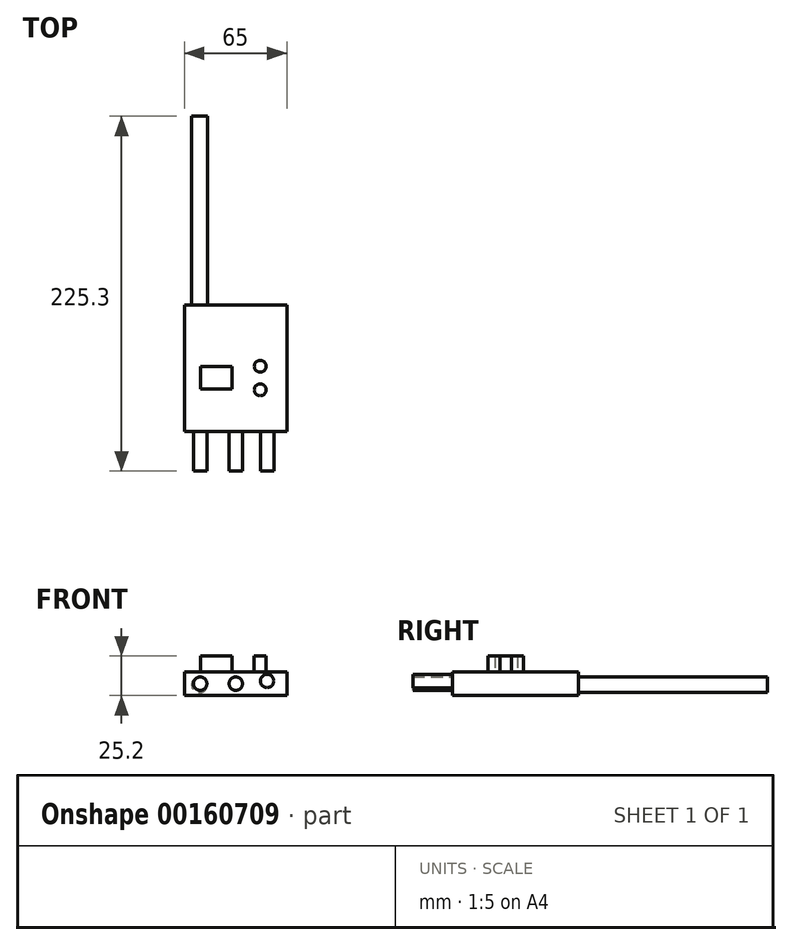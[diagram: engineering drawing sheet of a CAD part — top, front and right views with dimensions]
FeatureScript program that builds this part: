
annotation { "Feature Type Name" : "Feature", "Feature Type Description" : "" }
export const myFeature = defineFeature(function(context is Context, id is Id, definition is map)
    precondition{}
    {
        {
            var Q0;
            Q0=qCreatedBy(makeId("Top.planeOp"),FACE);
            var sketch = newSketch(context, id + "F0", { "sketchPlane" : qUnion([Q0])});
            skLineSegment(sketch, "E0.bottom", {"start": v(32.5, -40.15) * mm, "end": v(-32.5, -40.15) * mm});
            skLineSegment(sketch, "E0.top", {"start": v(32.5, 40.15) * mm, "end": v(-32.5, 40.15) * mm});
            skLineSegment(sketch, "E0.left", {"start": v(32.5, -40.15) * mm, "end": v(32.5, 40.15) * mm});
            skLineSegment(sketch, "E0.right", {"start": v(-32.5, -40.15) * mm, "end": v(-32.5, 40.15) * mm});
            skPoint(sketch, "E0.middle", {"position": v(0, 0) * mm});
            skSolve(sketch);
        }
        {
            var Q0;
            Q0=makeQuery(id+"F0.imprint","IMPRINT",FACE,{"disambiguationData":[TD([[makeQuery(id+"F0.imprint","IMPRINT",EDGE,{"derivedFrom":sQuery(id+"F0.wireOp",EDGE,"E0.bottom")}),-1.0]])]});
            extrude(context, id + "F1", {"entities" : qUnion([Q0]), "depth" : 15.2 * mm});
        }
        {
            var Q0;
            Q0=makeQuery(id+"F1.opExtrude","SWEPT_FACE",FACE,{"disambiguationData":[OSD([sQuery(id+"F0.wireOp",EDGE,"E0.top")])]});
            var sketch = newSketch(context, id + "F2", { "sketchPlane" : qUnion([Q0])});
            skCircle(sketch, "E1", {"center": v(23, 6.9) * mm, "radius": 5 * mm});
            skPoint(sketch, "E1.centerSnap0", {"position": v(32.5, 6.9) * mm});
            skSolve(sketch);
        }
        {
            var Q0;
            Q0=makeQuery(id+"F2.imprint","IMPRINT",FACE,{"disambiguationData":[TD([[makeQuery(id+"F2.imprint","IMPRINT",EDGE,{"derivedFrom":sQuery(id+"F2.wireOp",EDGE,"E1")}),1.0]])]});
            extrude(context, id + "F3", {"entities" : qUnion([Q0]), "operationType" : NewBodyOperationType.ADD, "depth" : 120 * mm});
        }
        {
            var Q0;
            Q0=makeQuery(id+"F1.opExtrude","SWEPT_FACE",FACE,{"disambiguationData":[OSD([sQuery(id+"F0.wireOp",EDGE,"E0.bottom")])]});
            var sketch = newSketch(context, id + "F4", { "sketchPlane" : qUnion([Q0])});
            skCircle(sketch, "E2", {"center": v(-22.6, 7.6) * mm, "radius": 4.25 * mm});
            skPoint(sketch, "E2.centerSnap0", {"position": v(-32.5, 7.6) * mm});
            skCircle(sketch, "E3", {"center": v(0, 7.6) * mm, "radius": 4.25 * mm});
            skCircle(sketch, "E4", {"center": v(19.9, 9.3) * mm, "radius": 4.25 * mm});
            skSolve(sketch);
        }
        {
            var Q0;
            Q0=makeQuery(id+"F4.imprint","IMPRINT",FACE,{"disambiguationData":[TD([[makeQuery(id+"F4.imprint","IMPRINT",EDGE,{"derivedFrom":sQuery(id+"F4.wireOp",EDGE,"E2")}),1.0]])]});
            var Q1;
            Q1=makeQuery(id+"F4.imprint","IMPRINT",FACE,{"disambiguationData":[TD([[makeQuery(id+"F4.imprint","IMPRINT",EDGE,{"derivedFrom":sQuery(id+"F4.wireOp",EDGE,"E3")}),1.0]])]});
            var Q2;
            Q2=makeQuery(id+"F4.imprint","IMPRINT",FACE,{"disambiguationData":[TD([[makeQuery(id+"F4.imprint","IMPRINT",EDGE,{"derivedFrom":sQuery(id+"F4.wireOp",EDGE,"E4")}),1.0]])]});
            extrude(context, id + "F5", {"entities" : qUnion([Q0, Q1, Q2]), "operationType" : NewBodyOperationType.ADD, "depth" : 25 * mm});
        }
        {
            var Q0;
            Q0=makeQuery(id+"F1.opExtrude","CAP_FACE",FACE,{"disambiguationData":[OSD([sQuery(id+"F0.wireOp",EDGE,"E0.bottom"),sQuery(id+"F0.wireOp",EDGE,"E0.top"),sQuery(id+"F0.wireOp",EDGE,"E0.left"),sQuery(id+"F0.wireOp",EDGE,"E0.right")])],"isStart":false});
            var sketch = newSketch(context, id + "F6", { "sketchPlane" : qUnion([Q0])});
            skLineSegment(sketch, "E5.bottom", {"start": v(-22.5, 1.35) * mm, "end": v(-2.5, 1.35) * mm});
            skLineSegment(sketch, "E5.top", {"start": v(-22.5, -13.15) * mm, "end": v(-2.5, -13.15) * mm});
            skLineSegment(sketch, "E5.left", {"start": v(-22.5, 1.35) * mm, "end": v(-22.5, -13.15) * mm});
            skLineSegment(sketch, "E5.right", {"start": v(-2.5, 1.35) * mm, "end": v(-2.5, -13.15) * mm});
            skCircle(sketch, "E6", {"center": v(15.5, 1.35) * mm, "radius": 3.75 * mm});
            skCircle(sketch, "E7", {"center": v(15.5, -13.65) * mm, "radius": 3.75 * mm});
            skSolve(sketch);
        }
        {
            var Q0;
            Q0=makeQuery(id+"F6.imprint","IMPRINT",FACE,{"disambiguationData":[TD([[makeQuery(id+"F6.imprint","IMPRINT",EDGE,{"derivedFrom":sQuery(id+"F6.wireOp",EDGE,"E5.bottom")}),-1.0]])]});
            var Q1;
            Q1=makeQuery(id+"F6.imprint","IMPRINT",FACE,{"disambiguationData":[TD([[makeQuery(id+"F6.imprint","IMPRINT",EDGE,{"derivedFrom":sQuery(id+"F6.wireOp",EDGE,"E6")}),1.0]])]});
            var Q2;
            Q2=makeQuery(id+"F6.imprint","IMPRINT",FACE,{"disambiguationData":[TD([[makeQuery(id+"F6.imprint","IMPRINT",EDGE,{"derivedFrom":sQuery(id+"F6.wireOp",EDGE,"E7")}),1.0]])]});
            extrude(context, id + "F7", {"entities" : qUnion([Q0, Q1, Q2]), "operationType" : NewBodyOperationType.ADD, "depth" : 10 * mm});
        }
    });
